# Revit family: VENTS-OVK
name_source: partatom
category: Mechanical Equipment
units: mm (PartAtom-declared; Revit-internal decimal feet)

## family parameters
Always vertical = Yes
Classification = None
Cut with Voids When Loaded = No
OmniClass Number = 23.75.35.17.11
OmniClass Title = Fans for Air Ductwork
Part Type = Breaks Into
Room Calculation Point = No
Round Connector Dimension = Use Diameter
Shared = No
Work Plane-Based = No

## types (44) — shared parameters
Casing Material = Metal Painted Black
Description = Low pressure axial fan in the steel casing for wall mounting
Distribution Box Material = Distribution Box
Family Version = 1.0
L1 = 10 mm  [stored 0.0328084 ft]
Load Classification = HVAC
Maintenance Zone Length = 600 mm
Maintenance Zone Material = Maintenance Zone
Manufacturer = Vents
Power Factor = 1
Protection rating = IPX4
URL = https://ventilation-system.com
r = 10 mm  [stored 0.0328084 ft]
sFl = 2 mm  [stored 0.00656168 ft]

## per-type parameters (varying)
| type | Apparent Power | Current | D | D2 | Din | H1 | L | L2 | Lgr | Maximum Air Flow | Model | Motor protection rating | Noise Level at 3 m (dBa) | Number of Poles | Power | RPM (min-1) | Transported Air Temperature (°C) | Type Comments | Voltage | Weight | dFl | gsD |
| OVK 2E 200 (50Hz) | 55 VA | 0 A | 210 mm | 280 mm | 206 mm  [stored 0.675853 ft] | 120 mm  [stored 0.393701 ft] | 60 mm  [stored 0.19685 ft] | 50 mm  [stored 0.164042 ft] | 2 mm  [stored 0.00656168 ft] | 860 m³/h | OVK 2E 200 | IP24 | 48 | 1 | 55 W | 2300 | -30...+60 | Axial fan for wall mounting OVK 2E 200 | 230 V | 2.80 kg | 35 mm  [stored 0.114829 ft] | 48 mm  [stored 0.15748 ft] |
| OVK 2E 200 (60Hz) | 61 VA | 0 A | 210 mm | 280 mm | 206 mm  [stored 0.675853 ft] | 120 mm  [stored 0.393701 ft] | 60 mm  [stored 0.19685 ft] | 50 mm  [stored 0.164042 ft] | 2 mm  [stored 0.00656168 ft] | 875 m³/h | OVK 2E 200 | IP24 | 49 | 1 | 61 W | 2550 | -30...+50 | Axial fan for wall mounting OVK 2E 200 | 230 V | 2.80 kg | 35 mm  [stored 0.114829 ft] | 48 mm  [stored 0.15748 ft] |
| OVK 2E 250 (50Hz) | 80 VA | 0 A | 260 mm | 340 mm | 256 mm | 130 mm  [stored 0.426509 ft] | 70 mm  [stored 0.229659 ft] | 60 mm  [stored 0.19685 ft] | 2 mm  [stored 0.00656168 ft] | 1050 m³/h | OVK 2E 250 | IP24 | 50 | 1 | 80 W | 2400 | -30...+60 | Axial fan for wall mounting OVK 2E 250 | 230 V | 3.80 kg | 40 mm  [stored 0.131234 ft] | 56 mm  [stored 0.183727 ft] |
| OVK 2E 250 (60Hz) | 91 VA | 0 A | 260 mm | 340 mm | 256 mm | 130 mm  [stored 0.426509 ft] | 70 mm  [stored 0.229659 ft] | 60 mm  [stored 0.19685 ft] | 2 mm  [stored 0.00656168 ft] | 1150 m³/h | OVK 2E 250 | IP24 | 51 | 1 | 91 W | 2990 | -30...+50 | Axial fan for wall mounting OVK 2E 250 | 230 V | 3.80 kg | 40 mm  [stored 0.131234 ft] | 56 mm  [stored 0.183727 ft] |
| OVK 4E 250 (50Hz) | 50 VA | 0 A | 260 mm | 340 mm | 256 mm | 130 mm  [stored 0.426509 ft] | 70 mm  [stored 0.229659 ft] | 60 mm  [stored 0.19685 ft] | 2 mm  [stored 0.00656168 ft] | 800 m³/h | OVK 4E 250 | IP24 | 38 | 1 | 50 W | 1380 | -30...+60 | Axial fan for wall mounting OVK 4E 250 | 230 V | 3.40 kg | 40 mm  [stored 0.131234 ft] | 56 mm  [stored 0.183727 ft] |
| OVK 4E 250 (60Hz) | 56 VA | 0 A | 260 mm | 340 mm | 256 mm | 130 mm  [stored 0.426509 ft] | 70 mm  [stored 0.229659 ft] | 60 mm  [stored 0.19685 ft] | 2 mm  [stored 0.00656168 ft] | 865 m³/h | OVK 4E 250 | IP24 | 39 | 1 | 56 W | 1730 | -30...+50 | Axial fan for wall mounting OVK 4E 250 | 230 V | 3.40 kg | 40 mm  [stored 0.131234 ft] | 56 mm  [stored 0.183727 ft] |
| OVK 2E 300 (50Hz) | 145 VA | 1 A | 317 mm | 397 mm | 313 mm | 140 mm  [stored 0.459318 ft] | 80 mm  [stored 0.262467 ft] | 70 mm  [stored 0.229659 ft] | 2 mm  [stored 0.00656168 ft] | 2230 m³/h | OVK 2E 300 | IP24 | 53 | 1 | 145 W | 2300 | -30...+60 | Axial fan for wall mounting OVK 2E 300 | 230 V | 5.90 kg | 40 mm  [stored 0.131234 ft] | 64 mm  [stored 0.209974 ft] |
| OVK 2E 300 (60Hz) | 178 VA | 1 A | 317 mm | 397 mm | 313 mm | 140 mm  [stored 0.459318 ft] | 80 mm  [stored 0.262467 ft] | 70 mm  [stored 0.229659 ft] | 2 mm  [stored 0.00656168 ft] | 2280 m³/h | OVK 2E 300 | IP24 | 54 | 1 | 178 W | 2410 | -30...+50 | Axial fan for wall mounting OVK 2E 300 | 230 V | 5.90 kg | 40 mm  [stored 0.131234 ft] | 64 mm  [stored 0.209974 ft] |
| OVK 4E 300 (50Hz) | 75 VA | 0 A | 317 mm | 397 mm | 313 mm | 140 mm  [stored 0.459318 ft] | 80 mm  [stored 0.262467 ft] | 70 mm  [stored 0.229659 ft] | 2 mm  [stored 0.00656168 ft] | 1340 m³/h | OVK 4E 300 | IP24 | 44 | 1 | 75 W | 1350 | -30...+60 | Axial fan for wall mounting OVK 4E 300 | 230 V | 5.00 kg | 40 mm  [stored 0.131234 ft] | 64 mm  [stored 0.209974 ft] |
| OVK 4E 300 (60Hz) | 92 VA | 0 A | 317 mm | 397 mm | 313 mm | 140 mm  [stored 0.459318 ft] | 80 mm  [stored 0.262467 ft] | 70 mm  [stored 0.229659 ft] | 2 mm  [stored 0.00656168 ft] | 1475 m³/h | OVK 4E 300 | IP24 | 45 | 1 | 92 W | 1405 | -30...+50 | Axial fan for wall mounting OVK 4E 300 | 230 V | 5.00 kg | 40 mm  [stored 0.131234 ft] | 64 mm  [stored 0.209974 ft] |
| OVK 4E 350 (50Hz) | 140 VA | 1 A | 374 mm | 460 mm | 370 mm | 160 mm  [stored 0.524934 ft] | 97 mm  [stored 0.318241 ft] | 87 mm  [stored 0.285433 ft] | 2 mm  [stored 0.00656168 ft] | 2500 m³/h | OVK 4E 350 | IP24 | 46 | 1 | 140 W | 1380 | -30...+60 | Axial fan for wall mounting OVK 4E 350 | 230 V | 7.50 kg | 43 mm  [stored 0.141076 ft] | 78 mm |
| OVK 4E 350 (60Hz) | 147 VA | 1 A | 374 mm | 460 mm | 370 mm | 160 mm  [stored 0.524934 ft] | 97 mm  [stored 0.318241 ft] | 87 mm  [stored 0.285433 ft] | 2 mm  [stored 0.00656168 ft] | 2650 m³/h | OVK 4E 350 | IP24 | 47 | 1 | 147 W | 1700 | -30...+50 | Axial fan for wall mounting OVK 4E 350 | 230 V | 7.70 kg | 43 mm  [stored 0.141076 ft] | 78 mm |
| OVK 4E 400 (50Hz) | 180 VA | 1 A | 416 mm | 528 mm | 412 mm | 195 mm  [stored 0.639764 ft] | 97 mm  [stored 0.318241 ft] | 87 mm  [stored 0.285433 ft] | 35 mm  [stored 0.114829 ft] | 3580 m³/h | OVK 4E 400 | IP24 | 53 | 1 | 180 W | 1380 | -30...+60 | Axial fan for wall mounting OVK 4E 400 | 230 V | 8.50 kg | 56 mm  [stored 0.183727 ft] | 78 mm |
| OVK 4E 400 (60Hz) | 240 VA | 1 A | 416 mm | 528 mm | 412 mm | 195 mm  [stored 0.639764 ft] | 97 mm  [stored 0.318241 ft] | 87 mm  [stored 0.285433 ft] | 35 mm  [stored 0.114829 ft] | 3890 m³/h | OVK 4E 400 | IP24 | 54 | 1 | 240 W | 1655 | -30...+50 | Axial fan for wall mounting OVK 4E 400 | 230 V | 8.50 kg | 56 mm  [stored 0.183727 ft] | 78 mm |
| OVK 4E 450 (50Hz) | 250 VA | 1 A | 465 mm | 607 mm | 461 mm | 205 mm  [stored 0.672572 ft] | 110 mm  [stored 0.360892 ft] | 100 mm  [stored 0.328084 ft] | 35 mm  [stored 0.114829 ft] | 4680 m³/h | OVK 4E 450 | IP24 | 56 | 1 | 250 W | 1350 | -30...+60 | Axial fan for wall mounting OVK 4E 450 | 230 V | 10.00 kg | 71 mm  [stored 0.23294 ft] | 88 mm |
| OVK 4E 450 (60Hz) | 325 VA | 1 A | 465 mm | 607 mm | 461 mm | 205 mm  [stored 0.672572 ft] | 110 mm  [stored 0.360892 ft] | 100 mm  [stored 0.328084 ft] | 35 mm  [stored 0.114829 ft] | 4790 m³/h | OVK 4E 450 | IP24 | 57 | 1 | 325 W | 1600 | -30...+50 | Axial fan for wall mounting OVK 4E 450 | 230 V | 10.00 kg | 71 mm  [stored 0.23294 ft] | 88 mm |
| OVK 4E 500 (50Hz) | 420 VA | 2 A | 520 mm | 655 mm | 516 mm | 205 mm  [stored 0.672572 ft] | 130 mm  [stored 0.426509 ft] | 120 mm  [stored 0.393701 ft] | 15 mm  [stored 0.0492126 ft] | 7060 m³/h | OVK 4E 500 | IP24 | 58 | 1 | 420 W | 1300 | -30...+60 | Axial fan for wall mounting OVK 4E 500 | 230 V | 14.00 kg | 68 mm  [stored 0.223097 ft] | 104 mm |
| OVK 4E 500 (60Hz) | 455 VA | 2 A | 520 mm | 655 mm | 516 mm | 205 mm  [stored 0.672572 ft] | 130 mm  [stored 0.426509 ft] | 120 mm  [stored 0.393701 ft] | 15 mm  [stored 0.0492126 ft] | 7130 m³/h | OVK 4E 500 | IP24 | 59 | 1 | 455 W | 1630 | -30...+50 | Axial fan for wall mounting OVK 4E 500 | 230 V | 14.00 kg | 68 mm  [stored 0.223097 ft] | 104 mm |
| OVK 4E 550 (50Hz) | 550 VA | 3 A | 570 mm | 710 mm | 566 mm | 215 mm | 140 mm  [stored 0.459318 ft] | 130 mm  [stored 0.426509 ft] | 15 mm  [stored 0.0492126 ft] | 8800 m³/h | OVK 4E 550 | IP24 | 62 | 1 | 550 W | 1300 | -30...+60 | Axial fan for wall mounting OVK 4E 550 | 230 V | 16.50 kg | 70 mm  [stored 0.229659 ft] | 112 mm  [stored 0.367454 ft] |
| OVK 4E 550 (60Hz) | 654 VA | 3 A | 570 mm | 710 mm | 566 mm | 215 mm | 140 mm  [stored 0.459318 ft] | 130 mm  [stored 0.426509 ft] | 15 mm  [stored 0.0492126 ft] | 8970 m³/h | OVK 4E 550 | IP24 | 63 | 1 | 654 W | 1580 | -30...+50 | Axial fan for wall mounting OVK 4E 550 | 230 V | 16.50 kg | 70 mm  [stored 0.229659 ft] | 112 mm  [stored 0.367454 ft] |
| OVK 4E 630 (50Hz) | 750 VA | 4 A | 650 mm | 800 mm | 646 mm | 230 mm | 154 mm  [stored 0.505249 ft] | 144 mm | 15 mm  [stored 0.0492126 ft] | 11900 m³/h | OVK 4E 630 | IP24 | 67 | 1 | 750 W | 1360 | -30...+60 | Axial fan for wall mounting OVK 4E 630 | 230 V | 20.00 kg | 75 mm | 123 mm |
| OVK 4E 630 (60Hz) | 979 VA | 4 A | 650 mm | 800 mm | 646 mm | 230 mm | 154 mm  [stored 0.505249 ft] | 144 mm | 15 mm  [stored 0.0492126 ft] | 12100 m³/h | OVK 4E 630 | IP24 | 68 | 1 | 979 W | 1625 | -30...+50 | Axial fan for wall mounting OVK 4E 630 | 230 V | 20.00 kg | 75 mm | 123 mm |
| OVK 2D 250 (50Hz) | 80 VA | 0 A | 260 mm | 340 mm | 256 mm | 130 mm  [stored 0.426509 ft] | 70 mm  [stored 0.229659 ft] | 60 mm  [stored 0.19685 ft] | 2 mm  [stored 0.00656168 ft] | 1060 m³/h | OVK 2D 250 | IP44 | 51 | 3 | 80 W | 2600 | -30...+60 | Axial fan for wall mounting OVK 2D 250 | 400 V | 3.80 kg | 40 mm  [stored 0.131234 ft] | 56 mm  [stored 0.183727 ft] |
| OVK 2D 250 (60Hz) | 92 VA | 0 A | 260 mm | 340 mm | 256 mm | 130 mm  [stored 0.426509 ft] | 70 mm  [stored 0.229659 ft] | 60 mm  [stored 0.19685 ft] | 2 mm  [stored 0.00656168 ft] | 1150 m³/h | OVK 2D 250 | IP44 | 52 | 3 | 92 W | 3030 | -30...+50 | Axial fan for wall mounting OVK 2D 250 | 400 V | 3.80 kg | 40 mm  [stored 0.131234 ft] | 56 mm  [stored 0.183727 ft] |
| OVK 4D 250 (50Hz) | 60 VA | 0 A | 260 mm | 340 mm | 256 mm | 130 mm  [stored 0.426509 ft] | 70 mm  [stored 0.229659 ft] | 60 mm  [stored 0.19685 ft] | 2 mm  [stored 0.00656168 ft] | 850 m³/h | OVK 4D 250 | IP44 | 38 | 3 | 60 W | 1400 | -30...+60 | Axial fan for wall mounting OVK 4D 250 | 400 V | 3.40 kg | 40 mm  [stored 0.131234 ft] | 56 mm  [stored 0.183727 ft] |
| OVK 4D 250 (60Hz) | 89 VA | 0 A | 260 mm | 340 mm | 256 mm | 130 mm  [stored 0.426509 ft] | 70 mm  [stored 0.229659 ft] | 60 mm  [stored 0.19685 ft] | 2 mm  [stored 0.00656168 ft] | 885 m³/h | OVK 4D 250 | IP44 | 38 | 3 | 89 W | 1750 | -30...+50 | Axial fan for wall mounting OVK 4D 250 | 400 V | 3.40 kg | 40 mm  [stored 0.131234 ft] | 56 mm  [stored 0.183727 ft] |
| OVK 2D 300 (50Hz) | 145 VA | 0 A | 317 mm | 397 mm | 313 mm | 140 mm  [stored 0.459318 ft] | 80 mm  [stored 0.262467 ft] | 70 mm  [stored 0.229659 ft] | 2 mm  [stored 0.00656168 ft] | 2310 m³/h | OVK 2D 300 | IP44 | 52 | 3 | 145 W | 2350 | -30...+60 | Axial fan for wall mounting OVK 2D 300 | 400 V | 5.10 kg | 40 mm  [stored 0.131234 ft] | 64 mm  [stored 0.209974 ft] |
| OVK 2D 300 (60Hz) | 165 VA | 0 A | 317 mm | 397 mm | 313 mm | 140 mm  [stored 0.459318 ft] | 80 mm  [stored 0.262467 ft] | 70 mm  [stored 0.229659 ft] | 2 mm  [stored 0.00656168 ft] | 2390 m³/h | OVK 2D 300 | IP44 | 52 | 3 | 165 W | 2570 | -30...+50 | Axial fan for wall mounting OVK 2D 300 | 400 V | 5.10 kg | 40 mm  [stored 0.131234 ft] | 64 mm  [stored 0.209974 ft] |
| OVK 4D 300 (50Hz) | 75 VA | 0 A | 317 mm | 397 mm | 313 mm | 140 mm  [stored 0.459318 ft] | 80 mm  [stored 0.262467 ft] | 70 mm  [stored 0.229659 ft] | 2 mm  [stored 0.00656168 ft] | 1310 m³/h | OVK 4D 300 | IP44 | 45 | 3 | 75 W | 1380 | -30...+60 | Axial fan for wall mounting OVK 4D 300 | 400 V | 5.10 kg | 40 mm  [stored 0.131234 ft] | 64 mm  [stored 0.209974 ft] |
| OVK 4D 300 (60Hz) | 94 VA | 0 A | 317 mm | 397 mm | 313 mm | 140 mm  [stored 0.459318 ft] | 80 mm  [stored 0.262467 ft] | 70 mm  [stored 0.229659 ft] | 2 mm  [stored 0.00656168 ft] | 1530 m³/h | OVK 4D 300 | IP44 | 45 | 3 | 94 W | 1640 | -30...+50 | Axial fan for wall mounting OVK 4D 300 | 400 V | 5.10 kg | 40 mm  [stored 0.131234 ft] | 64 mm  [stored 0.209974 ft] |
| OVK 4D 350 (50Hz) | 140 VA | 0 A | 374 mm | 460 mm | 370 mm | 160 mm  [stored 0.524934 ft] | 97 mm  [stored 0.318241 ft] | 87 mm  [stored 0.285433 ft] | 2 mm  [stored 0.00656168 ft] | 2520 m³/h | OVK 4D 350 | IP44 | 46 | 3 | 140 W | 1380 | -30...+60 | Axial fan for wall mounting OVK 4D 350 | 400 V | 7.50 kg | 43 mm  [stored 0.141076 ft] | 78 mm |
| OVK 4D 350 (60Hz) | 150 VA | 0 A | 374 mm | 460 mm | 370 mm | 160 mm  [stored 0.524934 ft] | 97 mm  [stored 0.318241 ft] | 87 mm  [stored 0.285433 ft] | 2 mm  [stored 0.00656168 ft] | 2590 m³/h | OVK 4D 350 | IP44 | 46 | 3 | 150 W | 1640 | -30...+50 | Axial fan for wall mounting OVK 4D 350 | 400 V | 7.50 kg | 43 mm  [stored 0.141076 ft] | 78 mm |
| OVK 4D 400 (50Hz) | 180 VA | 0 A | 416 mm | 528 mm | 412 mm | 195 mm  [stored 0.639764 ft] | 97 mm  [stored 0.318241 ft] | 87 mm  [stored 0.285433 ft] | 35 mm  [stored 0.114829 ft] | 3740 m³/h | OVK 4D 400 | IP44 | 54 | 3 | 180 W | 1380 | -30...+60 | Axial fan for wall mounting OVK 4D 400 | 400 V | 8.50 kg | 56 mm  [stored 0.183727 ft] | 78 mm |
| OVK 4D 400 (60Hz) | 195 VA | 1 A | 416 mm | 528 mm | 412 mm | 195 mm  [stored 0.639764 ft] | 97 mm  [stored 0.318241 ft] | 87 mm  [stored 0.285433 ft] | 35 mm  [stored 0.114829 ft] | 3870 m³/h | OVK 4D 400 | IP44 | 54 | 3 | 195 W | 1625 | -30...+50 | Axial fan for wall mounting OVK 4D 400 | 400 V | 8.50 kg | 56 mm  [stored 0.183727 ft] | 78 mm |
| OVK 4D 450 (50Hz) | 250 VA | 1 A | 465 mm | 607 mm | 461 mm | 205 mm  [stored 0.672572 ft] | 110 mm  [stored 0.360892 ft] | 100 mm  [stored 0.328084 ft] | 35 mm  [stored 0.114829 ft] | 5280 m³/h | OVK 4D 450 | IP44 | 56 | 3 | 250 W | 1360 | -30...+60 | Axial fan for wall mounting OVK 4D 450 | 400 V | 10.00 kg | 71 mm  [stored 0.23294 ft] | 88 mm |
| OVK 4D 450 (60Hz) | 275 VA | 1 A | 465 mm | 607 mm | 461 mm | 205 mm  [stored 0.672572 ft] | 110 mm  [stored 0.360892 ft] | 100 mm  [stored 0.328084 ft] | 35 mm  [stored 0.114829 ft] | 5350 m³/h | OVK 4D 450 | IP44 | 56 | 3 | 275 W | 1620 | -30...+50 | Axial fan for wall mounting OVK 4D 450 | 400 V | 10.00 kg | 71 mm  [stored 0.23294 ft] | 88 mm |
| OVK 4D 500 (50Hz) | 450 VA | 1 A | 520 mm | 655 mm | 516 mm | 250 mm | 130 mm  [stored 0.426509 ft] | 120 mm  [stored 0.393701 ft] | 60 mm  [stored 0.19685 ft] | 6570 m³/h | OVK 4D 500 | IP24 | 60 | 3 | 450 W | 1300 | -30..+60 | Axial fan for wall mounting OVK 4D 500 | 400 V | 14.00 kg | 68 mm  [stored 0.223097 ft] | 104 mm |
| OVK 4D 500 (60Hz) | 370 VA | 1 A | 520 mm | 655 mm | 516 mm | 250 mm | 130 mm  [stored 0.426509 ft] | 120 mm  [stored 0.393701 ft] | 60 mm  [stored 0.19685 ft] | 6230 m³/h | OVK 4D 500 | IP24 | 60 | 3 | 370 W | 1605 | -30..+50 | Axial fan for wall mounting OVK 4D 500 | 400 V | 14.00 kg | 68 mm  [stored 0.223097 ft] | 104 mm |
| OVK 4D 550 (50Hz) | 750 VA | 2 A | 570 mm | 710 mm | 566 mm | 260 mm | 140 mm  [stored 0.459318 ft] | 130 mm  [stored 0.426509 ft] | 60 mm  [stored 0.19685 ft] | 9700 m³/h | OVK 4D 550 | IP24 | 64 | 3 | 750 W | 1350 | -30..+60 | Axial fan for wall mounting OVK 4D 550 | 400 V | 16.50 kg | 70 mm  [stored 0.229659 ft] | 112 mm  [stored 0.367454 ft] |
| OVK 4D 550 (60Hz) | 600 VA | 1 A | 570 mm | 710 mm | 566 mm | 260 mm | 140 mm  [stored 0.459318 ft] | 130 mm  [stored 0.426509 ft] | 60 mm  [stored 0.19685 ft] | 7380 m³/h | OVK 4D 550 | IP24 | 64 | 3 | 600 W | 1605 | -30..+50 | Axial fan for wall mounting OVK 4D 550 | 400 V | 16.50 kg | 70 mm  [stored 0.229659 ft] | 112 mm  [stored 0.367454 ft] |
| OVK 4D 630 (50Hz) | 800 VA | 2 A | 650 mm | 800 mm | 646 mm | 275 mm | 154 mm  [stored 0.505249 ft] | 144 mm | 60 mm  [stored 0.19685 ft] | 12200 m³/h | OVK 4D 630 | IP24 | 69 | 3 | 800 W | 1320 | -30..+60 | Axial fan for wall mounting OVK 4D 630 | 400 V | 20.00 kg | 75 mm | 123 mm |
| OVK 4D 630 (60Hz) | 910 VA | 2 A | 650 mm | 800 mm | 646 mm | 275 mm | 154 mm  [stored 0.505249 ft] | 144 mm | 60 mm  [stored 0.19685 ft] | 12400 m³/h | OVK 4D 630 | IP24 | 69 | 3 | 910 W | 1585 | -30..+50 | Axial fan for wall mounting OVK 4D 630 | 400 V | 20.00 kg | 75 mm | 123 mm |
| OVK 6D 710 (50Hz) | 1150 VA | 2 A | 725 mm | 890 mm | 721 mm | 350 mm | 172 mm  [stored 0.564304 ft] | 162 mm | 180 mm  [stored 0.590551 ft] | 15440 m³/h | OVK 6D 710 | IP44 | 63 | 3 | 1150 W | 830 | -30...+60 | Axial fan for wall mounting OVK 6D 710 | 400 V | 31.00 kg | 83 mm | 138 mm |
| OVK 6D 800 (50Hz) | 1850 VA | 4 A | 800 mm | 970 mm | 796 mm | 350 mm | 172 mm  [stored 0.564304 ft] | 162 mm | 180 mm  [stored 0.590551 ft] | 25000 m³/h | OVK 6D 800 | IP44 | 67 | 3 | 1850 W | 915 | -30...+60 | Axial fan for wall mounting OVK 6D 800 | 400 V | 42.00 kg | 85 mm | 138 mm |

note: [stored X ft] marks values corroborated as IEEE doubles in the binary element streams (Revit-internal decimal feet)

## geometry (parser evidence)
native form markers: Sweep x12
no freeform markers — native parametric forms only
